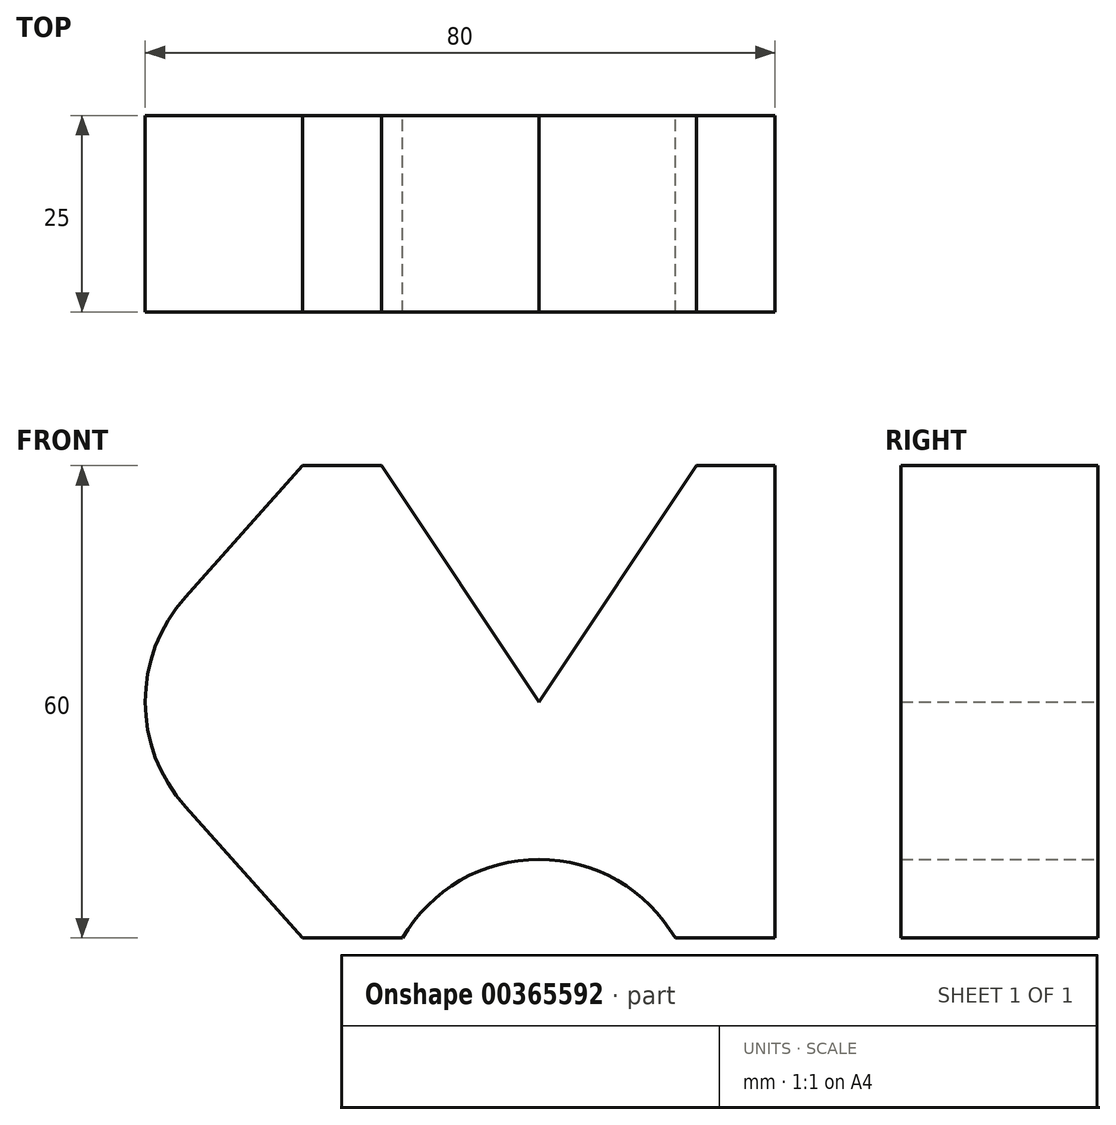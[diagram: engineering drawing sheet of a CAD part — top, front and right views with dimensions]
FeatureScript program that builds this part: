
annotation { "Feature Type Name" : "Feature", "Feature Type Description" : "" }
export const myFeature = defineFeature(function(context is Context, id is Id, definition is map)
    precondition{}
    {
        {
            var Q0;
            Q0=qCreatedBy(makeId("Front.planeOp"),FACE);
            var sketch = newSketch(context, id + "F0", { "sketchPlane" : qUnion([Q0])});
            skLineSegment(sketch, "E0", {"start": v(0, 0) * mm, "end": v(20, 30) * mm});
            skLineSegment(sketch, "E1", {"start": v(20, 30) * mm, "end": v(30, 30) * mm});
            skLineSegment(sketch, "E2", {"start": v(30, 30) * mm, "end": v(30, -30) * mm});
            skLineSegment(sketch, "E3", {"start": v(30, -30) * mm, "end": v(17.32, -30) * mm});
            skArc(sketch, "E4", {"start": v(17.32, -30) * mm, "mid": v(0, -20) * mm, "end": v(-17.32, -30) * mm});
            skLineSegment(sketch, "E5", {"start": v(-17.32, -30) * mm, "end": v(-30, -30) * mm});
            skLineSegment(sketch, "E6", {"start": v(-30, -30) * mm, "end": v(-44.9, -13.33) * mm});
            skLineSegment(sketch, "E7", {"start": v(0, 0) * mm, "end": v(-20, 30) * mm});
            skLineSegment(sketch, "E8", {"start": v(-20, 30) * mm, "end": v(-30, 30) * mm});
            skLineSegment(sketch, "E9", {"start": v(-30, 30) * mm, "end": v(-44.9, 13.33) * mm});
            skArc(sketch, "E10", {"start": v(-44.9, 13.33) * mm, "mid": v(-50, 0) * mm, "end": v(-44.9, -13.33) * mm});
            skLineSegment(sketch, "E11", {"start": v(-30, 30) * mm, "end": v(-30, -35.04) * mm, "construction": true});
            skSolve(sketch);
        }
        {
            var Q0;
            Q0=makeQuery(id+"F0.imprint","IMPRINT",FACE,{"disambiguationData":[TD([[makeQuery(id+"F0.imprint","IMPRINT",EDGE,{"derivedFrom":sQuery(id+"F0.wireOp",EDGE,"E0")}),-1.0]])]});
            extrude(context, id + "F1", {"entities" : qUnion([Q0]), "depth" : 25 * mm});
        }
    });
